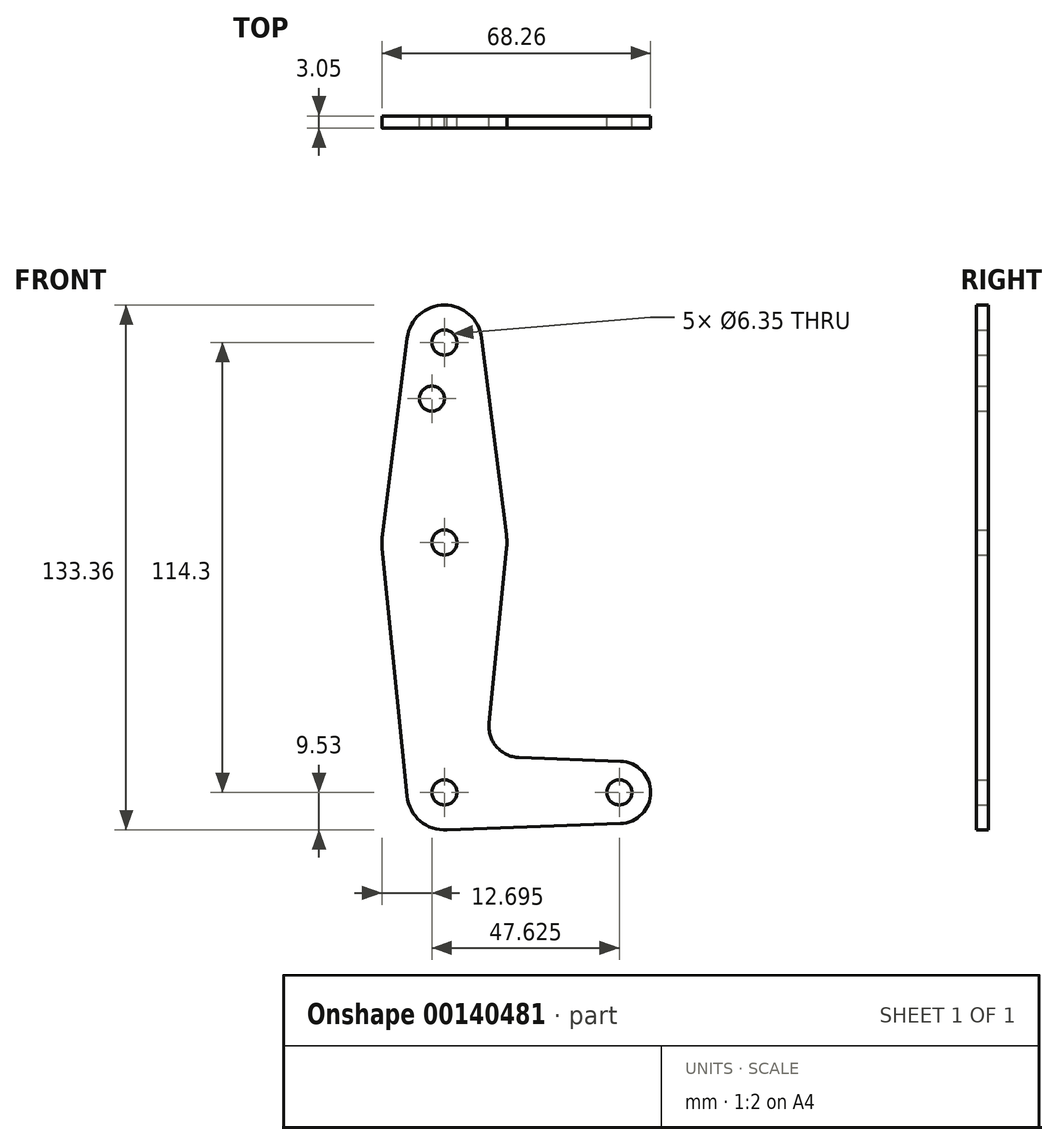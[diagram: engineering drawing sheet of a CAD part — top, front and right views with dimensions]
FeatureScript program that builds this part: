
annotation { "Feature Type Name" : "Feature", "Feature Type Description" : "" }
export const myFeature = defineFeature(function(context is Context, id is Id, definition is map)
    precondition{}
    {
        {
            var Q0;
            Q0=qCreatedBy(makeId("Front.planeOp"),FACE);
            var sketch = newSketch(context, id + "F0", { "sketchPlane" : qUnion([Q0])});
            skLineSegment(sketch, "E0", {"start": v(0, 0) * mm, "end": v(0, 63.5) * mm, "construction": true});
            skLineSegment(sketch, "E1", {"start": v(0, 63.5) * mm, "end": v(0, 114.3) * mm, "construction": true});
            skLineSegment(sketch, "E2", {"start": v(0, 0) * mm, "end": v(44.45, 0) * mm, "construction": true});
            skCircle(sketch, "E3", {"center": v(0, 114.3) * mm, "radius": 9.53 * mm});
            skCircle(sketch, "E4", {"center": v(0, 63.5) * mm, "radius": 15.88 * mm});
            skCircle(sketch, "E5", {"center": v(0, 0) * mm, "radius": 9.53 * mm});
            skCircle(sketch, "E6", {"center": v(44.45, 0) * mm, "radius": 7.94 * mm});
            skLineSegment(sketch, "E7", {"start": v(-9.45, 115.5) * mm, "end": v(-15.75, 65.48) * mm});
            skLineSegment(sketch, "E8", {"start": v(9.45, 115.5) * mm, "end": v(15.75, 65.48) * mm});
            skLineSegment(sketch, "E9", {"start": v(-15.8, 61.91) * mm, "end": v(-9.48, -0.95) * mm});
            skLineSegment(sketch, "E10", {"start": v(44.73, 7.93) * mm, "end": v(18.97, 8.85) * mm});
            skLineSegment(sketch, "E11", {"start": v(15.8, 61.91) * mm, "end": v(11.34, 17.6) * mm});
            skLineSegment(sketch, "E12", {"start": v(0, -9.53) * mm, "end": v(44.73, -7.93) * mm});
            skCircle(sketch, "E13", {"center": v(0, 114.3) * mm, "radius": 3.18 * mm});
            skCircle(sketch, "E14", {"center": v(0, 63.5) * mm, "radius": 3.18 * mm});
            skCircle(sketch, "E15", {"center": v(0, 0) * mm, "radius": 3.18 * mm});
            skCircle(sketch, "E16", {"center": v(44.45, 0) * mm, "radius": 3.18 * mm});
            skCircle(sketch, "E17", {"center": v(-3.18, 100.03) * mm, "radius": 3.18 * mm});
            skArc(sketch, "E18.filletArc", {"start": v(11.34, 17.6) * mm, "mid": v(13.26, 11.57) * mm, "end": v(18.97, 8.85) * mm});
            skSolve(sketch);
        }
        {
            var Q0;
            Q0 = qSketchRegion(id + "F0", true);
            extrude(context, id + "F1", {"entities" : qUnion([Q0]), "depth" : 3.05 * mm});
        }
    });
